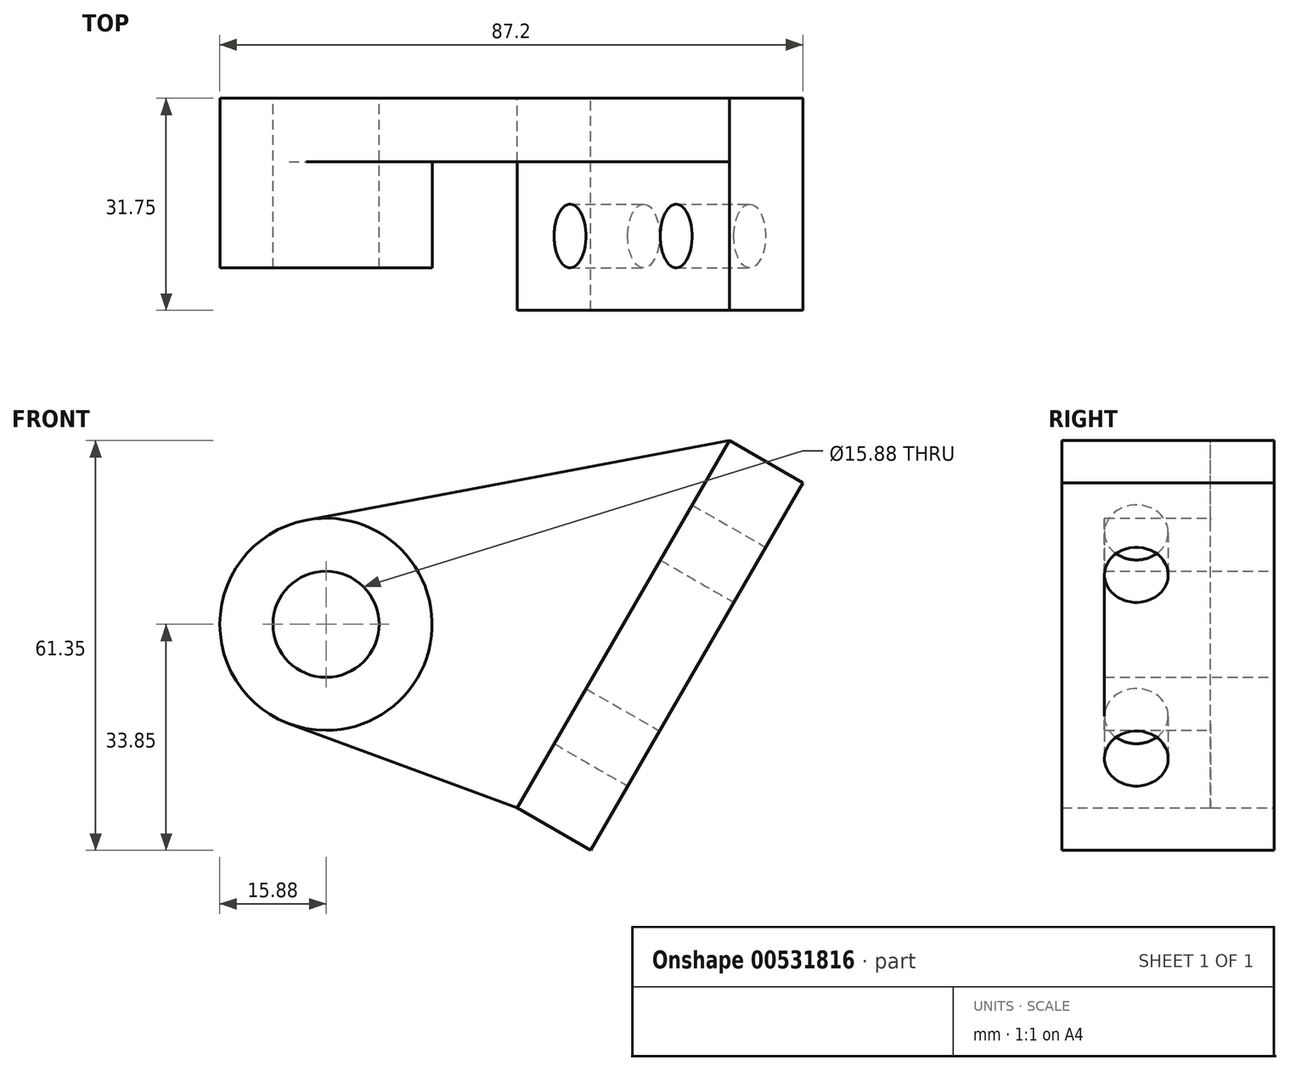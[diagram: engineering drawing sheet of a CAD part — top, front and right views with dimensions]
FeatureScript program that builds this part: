
annotation { "Feature Type Name" : "Feature", "Feature Type Description" : "" }
export const myFeature = defineFeature(function(context is Context, id is Id, definition is map)
    precondition{}
    {
        {
            var Q0;
            Q0=qCreatedBy(makeId("Front.planeOp"),FACE);
            var sketch = newSketch(context, id + "F0", { "sketchPlane" : qUnion([Q0])});
            skCircle(sketch, "E0", {"center": v(0, 0) * mm, "radius": 7.94 * mm});
            skCircle(sketch, "E1", {"center": v(0, 0) * mm, "radius": 15.88 * mm});
            skLineSegment(sketch, "E2", {"start": v(28.58, -27.5) * mm, "end": v(60.33, 27.5) * mm});
            skLineSegment(sketch, "E3", {"start": v(60.32, 27.5) * mm, "end": v(71.32, 21.15) * mm});
            skLineSegment(sketch, "E4", {"start": v(71.32, 21.15) * mm, "end": v(39.57, -33.85) * mm});
            skLineSegment(sketch, "E5", {"start": v(39.57, -33.85) * mm, "end": v(28.58, -27.5) * mm});
            skLineSegment(sketch, "E6", {"start": v(-5.5, -14.89) * mm, "end": v(28.58, -27.5) * mm});
            skLineSegment(sketch, "E7", {"start": v(-2.93, 15.6) * mm, "end": v(60.33, 27.5) * mm});
            skLineSegment(sketch, "E8", {"start": v(-44.57, 0) * mm, "end": v(109.16, 0) * mm, "construction": true});
            skPoint(sketch, "E9", {"position": v(44.45, 0) * mm});
            skLineSegment(sketch, "E10", {"start": v(44.45, 63.24) * mm, "end": v(44.45, -63.24) * mm, "construction": true});
            skSolve(sketch);
        }
        {
            var Q0;
            Q0=makeQuery(id+"F0.imprint","IMPRINT",FACE,{"disambiguationData":[TD([[makeQuery(id+"F0.imprint","IMPRINT",EDGE,{"derivedFrom":sQuery(id+"F0.wireOp",EDGE,"E2")}),1.0]])]});
            extrude(context, id + "F1", {"entities" : qUnion([Q0]), "depth" : 9.52 * mm, "offsetDistance" : 25.4 * mm});
        }
        {
            var Q0;
            Q0=makeQuery(id+"F0.imprint","IMPRINT",FACE,{"disambiguationData":[TD([[makeQuery(id+"F0.imprint","IMPRINT",EDGE,{"derivedFrom":sQuery(id+"F0.wireOp",EDGE,"E0")}),-1.0]])]});
            extrude(context, id + "F2", {"entities" : qUnion([Q0]), "operationType" : NewBodyOperationType.ADD, "depth" : 25.4 * mm, "offsetDistance" : 25.4 * mm});
        }
        {
            var Q0;
            Q0=makeQuery(id+"F0.imprint","IMPRINT",FACE,{"disambiguationData":[TD([[makeQuery(id+"F0.imprint","IMPRINT",EDGE,{"derivedFrom":sQuery(id+"F0.wireOp",EDGE,"E2")}),-1.0]])]});
            extrude(context, id + "F3", {"entities" : qUnion([Q0]), "operationType" : NewBodyOperationType.ADD, "depth" : 31.75 * mm, "offsetDistance" : 25.4 * mm});
        }
        {
            var Q0;
            Q0=makeQuery(id+"F3.opExtrude","SWEPT_FACE",FACE,{"disambiguationData":[OSD([sQuery(id+"F0.wireOp",EDGE,"E4")])]});
            var sketch = newSketch(context, id + "F4", { "sketchPlane" : qUnion([Q0])});
            skCircle(sketch, "E11", {"center": v(-20.64, 6.35) * mm, "radius": 4.76 * mm});
            skCircle(sketch, "E12", {"center": v(-20.64, 38.1) * mm, "radius": 4.76 * mm});
            skSolve(sketch);
        }
        {
            var Q0;
            Q0=sQuery(id+"F4.wireOp",VERTEX,"E11.center");
            var Q1;
            Q1=sQuery(id+"F4.wireOp",VERTEX,"E12.center");
            var Q2;
            Q2=makeQuery(id+"F1.opExtrude","SWEPT_BODY",BODY,{"disambiguationData":[OSD([sQuery(id+"F0.wireOp",EDGE,"E1"),sQuery(id+"F0.wireOp",EDGE,"E2"),sQuery(id+"F0.wireOp",EDGE,"E6"),sQuery(id+"F0.wireOp",EDGE,"E7")])]});
            hole(context, id + "F5", {"style" : HoleStyle.SIMPLE, "endStyle" : HoleEndStyle.BLIND, "holeDiameter" : 9.52 * mm, "holeDepth" : 12.7 * mm, "isTappedThrough" : true, "tappedDepth" : 12.7 * mm, "tapClearance" : 3, "locations" : qUnion([Q0, Q1]), "scope" : qUnion([Q2])});
        }
    });
